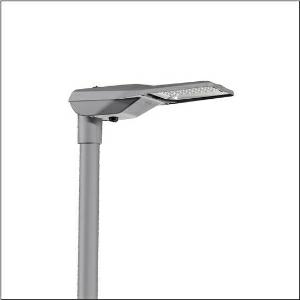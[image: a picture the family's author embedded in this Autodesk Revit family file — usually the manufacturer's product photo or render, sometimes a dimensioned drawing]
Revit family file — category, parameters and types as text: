
# Revit family: streetlight_sl_21_mini___st0_5a_5xe2b33t08gb_0718
name_source: partatom
category: Lighting Fixtures
units: mm (PartAtom-declared; Revit-internal decimal feet)

## family parameters
Cut with Voids When Loaded = No
Host = Face
Light Source = No
Part Type = Normal
Room Calculation Point = No
Round Connector Dimension = Use Diameter
Shared = No

## types (1)
- --- (1 x LED, 5940 lm, 40.4 W, 3000K)
    Apparent Load = 40 VA
    CIE Flux Codes = 41 75 97 100 100
    Color Rendering = 70
    Color Temperature = 3000K
    Default Elevation = 1800 mm
    Description = Streetlight SL 21 mini, mast luminaire, primary light control with lens, of PMMA, primary optical cover: cover, of toughened safety glass, transparent, light distribution: ST0.5a, light emission: direct distribution, primary light characteristic: asymmetric, installation type: side-entry, post-top, LED, High Power LED, rated luminous flux: 5.940lm, luminous efficacy: 147lm/W, light colour: 730, colour temperature: 3000K, control gear: D4i, control: overheat protection, constant luminous flux control, time-dependent luminous flux control, flexible luminous flux parameterisation, pre-setting: logarithmic dimming characteristic, mains connection: 220..240V, AC, 50/60Hz, start of lifetime: 40W, end of service life: 41W, reduction: 19W, luminaire housing, of diecast aluminium, powder-coated, SITECO metallic grey (DB 702S), corrosivity category C5 high according to DIN EN ISO 12944, please order mast flange separately, inclination adjustable: 0°, 5°, 10°, 15°, sealing non-destructively replaceable, multi-level sealing system, length: 628mm, width: 235mm, height: 110mm, mast flange for spigot size: 42mm (side-entry): 5XC10008XM4, 60/48mm (side-entry/post-top): 5XC10108XM2, 76/60mm (side-entry/post-top): 5XC10108XM1, mounting height: 4..8m, Smart Interface below and above, protection rating (complete): IP66, insulation class (complete): insulation class II (safety insulation), certification: CE, ENEC, ENEC+, VDE, impact resistance: IK10, permissible operating ambient temperature for outdoor applications: -40..+50°C, standard-compliant lighting for roads and squares, packaging unit: 1 piece

Light Distribution: ST0.5a
    Height = 110 mm
    Lamp = 1 x LED
    Lamp Light Flux = 5940 lm
    Lamp Power = 40.4 W
    Lamp count = 1
    Length = 625 mm
    Luminous efficacy = 147 lm/W
    Manufacturer = Siteco
    ModVariant = No
    Model = 5XE2B33T08GB
    Number of Poles = 1
    OnlyDefault = Yes
    Power Factor = 1
    Product Name = Streetlight SL 21 mini | ST0.5a
    Product group = mast luminaire | pylon top
    ProductGroupID = 6100
    Protection Class = Protection class II
    Protection Degree = IP 66
    RLX_Detail_Level = 1
    RLX_Emergency_Light_Flux = 0 lm
    RLX_Emergency_Type = 0
    RLX_Emergency_Type_DB = No
    RlxData = <blob elided: 37341 chars, md5=71ccc2f6>
    Socket = socket
    Standby Power = 0 W
    System Light Flux = 5940 lm
    System Power = 40 W
    Type Comments = factory setting: luminous flux: 100 % | dim-lin: 254 | 812 mA
    Type Image = l_1003514.jpg
    URL = http://relux.com
    VarID = @adj_188577
    Voltage = 0 V
    Weight = 0.00 kg
    Width = 234 mm

## geometry (parser evidence)
native form markers: Blend x4, Sweep x11
no freeform markers — native parametric forms only
